# Revit family: Legrand Caja Plexo³ 12 módulos
name_source: partatom
category: Equipement électrique
revit_build: Autodesk Revit 2018 (Build: 20170223_1515(x64)
units: mm (PartAtom-declared; Revit-internal decimal feet)

## family parameters
Basée sur le plan de construction = Non
Configuration du panneau = Deux colonnes, circuits au sein
Cote de connecteur circulaire = Utiliser le diamètre
Couper avec des vides une fois chargée = Non
Numéro OmniClass = 23.80.30.11.17
Partagée = Non
Point de calcul de pièce = Non
Titre OmniClass = Distribution Boards and Control Panels
Toujours verticalement = Oui
Type d'élément = Tableau de raccordement

## types (16) — shared parameters
Condiciones Generales de Uso = https://export.legrand.com
ETIM Class 6.0 = EC000214
Fabricant = Legrand
IK = 09
IP = 65
Image du type = Plexo3_12_modules_001922_pw_153883_pz_0.jpg
Materia = Poliestireno
Poliestireno
RAL = 7046
URL = www.legrand.fr

## per-type parameters (varying)
| type | Bornas N | Bornas T | Caja 001921 | Caja 001922 | Caja 001923 | Caja 601831 | Caja 601832 | Caja 601833 | Caja 601940 | Caja 601941 | Caja 601942 | Caja 601943 | Caja 601961 | Caja 601962 | Caja 601963 | Caja 601981 | Caja 601982 | Caja 601983 |
| Plexo³ 12 módulos de 1 fila 001921 |  | terminal 5+9 hoyos | Oui | Non | Non | Non | Non | Non | Non | Non | Non | Non | Non | Non | Non | Non | Non | Non |
| Plexo³ 12 módulos de 2 filas 001922 |  | terminal 5+18 hoyos | Non | Oui | Non | Non | Non | Non | Non | Non | Non | Non | Non | Non | Non | Non | Non | Non |
| Plexo³ 12 módulos de 3 filas 001923 |  | terminal 5+27 hoyos | Non | Non | Oui | Non | Non | Non | Non | Non | Non | Non | Non | Non | Non | Non | Non | Non |
| Plexo³ 12 módulos de 1 fila 601831 |  | terminal 5+9 hoyos | Non | Non | Non | Oui | Non | Non | Non | Non | Non | Non | Non | Non | Non | Non | Non | Non |
| Plexo³ 12 módulos de 1 fila 601940 |  |  | Non | Non | Non | Non | Non | Non | Oui | Non | Non | Non | Non | Non | Non | Non | Non | Non |
| Plexo³ 12 módulos de 1 fila 601941 | terminal 8 hoyos | terminal 13 hoyos | Non | Non | Non | Non | Non | Non | Non | Oui | Non | Non | Non | Non | Non | Non | Non | Non |
| Plexo³ 12 módulos de 1 fila 601961 |  | terminal 13 hoyos | Non | Non | Non | Non | Non | Non | Non | Non | Non | Non | Oui | Non | Non | Non | Non | Non |
| Plexo³ 12 módulos de 1 fila 601981 | terminal 13 hoyos | terminal 13 hoyos | Non | Non | Non | Non | Non | Non | Non | Non | Non | Non | Non | Non | Non | Oui | Non | Non |
| Plexo³ 12 módulos de 2 filas 601832 |  | terminal 5+18 hoyos | Non | Non | Non | Non | Oui | Non | Non | Non | Non | Non | Non | Non | Non | Non | Non | Non |
| Plexo³ 12 módulos de 2 filas 601942 |  |  | Non | Non | Non | Non | Non | Non | Non | Non | Oui | Non | Non | Non | Non | Non | Non | Non |
| Plexo³ 12 módulos de 2 filas 601962 |  | terminal 17 hoyos | Non | Non | Non | Non | Non | Non | Non | Non | Non | Non | Non | Oui | Non | Non | Non | Non |
| Plexo³ 12 módulos de 2 filas 601982 | terminal 17 hoyos | terminal 17 hoyos | Non | Non | Non | Non | Non | Non | Non | Non | Non | Non | Non | Non | Non | Non | Oui | Non |
| Plexo³ 12 módulos de 3 filas 601833 |  | terminal 5+27 hoyos | Non | Non | Non | Non | Non | Oui | Non | Non | Non | Non | Non | Non | Non | Non | Non | Non |
| Plexo³ 12 módulos de 3 filas 601943 |  |  | Non | Non | Non | Non | Non | Non | Non | Non | Non | Oui | Non | Non | Non | Non | Non | Non |
| Plexo³ 12 módulos de 3 filas 601963 |  | terminal 22 hoyos | Non | Non | Non | Non | Non | Non | Non | Non | Non | Non | Non | Non | Oui | Non | Non | Non |
| Plexo³ 12 módulos de 3 filas 601983 | terminal 22 hoyos | terminal 22 hoyos | Non | Non | Non | Non | Non | Non | Non | Non | Non | Non | Non | Non | Non | Non | Non | Oui |

note: column(s) folded — value = type name in every type: Description
